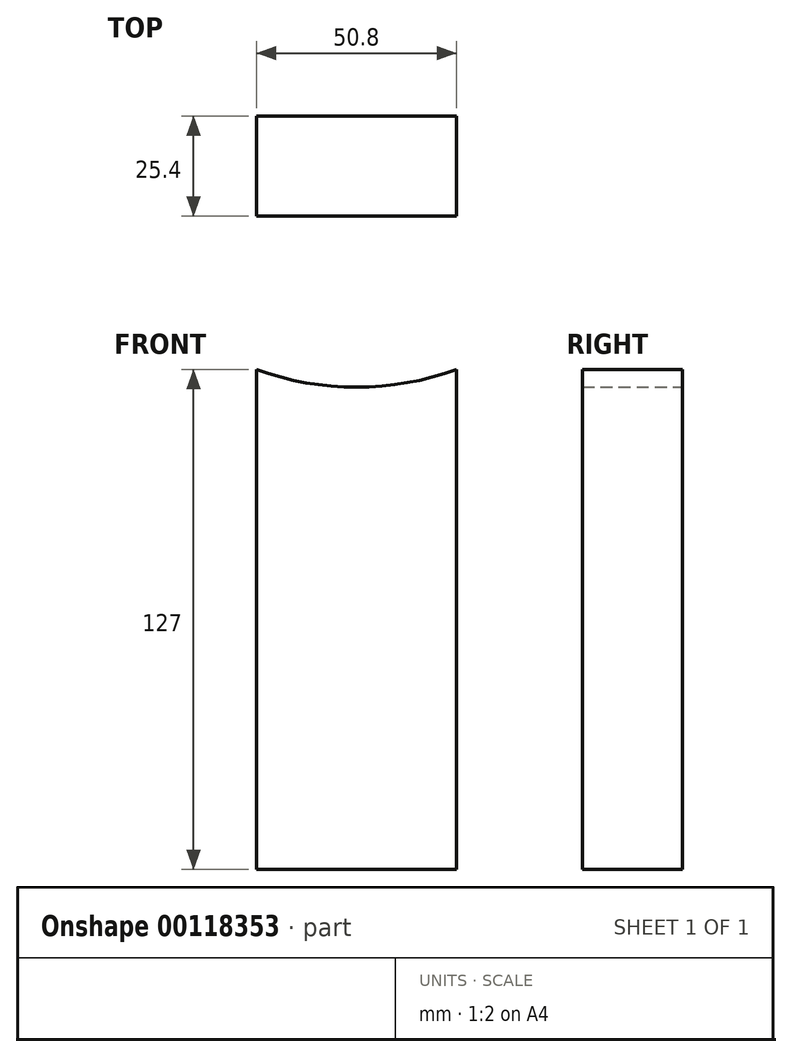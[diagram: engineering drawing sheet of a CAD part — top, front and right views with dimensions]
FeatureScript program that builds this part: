
annotation { "Feature Type Name" : "Feature", "Feature Type Description" : "" }
export const myFeature = defineFeature(function(context is Context, id is Id, definition is map)
    precondition{}
    {
        {
            var Q0;
            Q0=qCreatedBy(makeId("Front.planeOp"),FACE);
            var sketch = newSketch(context, id + "F0", { "sketchPlane" : qUnion([Q0])});
            skLineSegment(sketch, "E0.top", {"start": v(-41.57, -90.75) * mm, "end": v(9.23, -90.75) * mm});
            skLineSegment(sketch, "E0.left", {"start": v(-41.57, 36.25) * mm, "end": v(-41.57, -90.75) * mm});
            skLineSegment(sketch, "E0.right", {"start": v(9.23, 36.25) * mm, "end": v(9.23, -90.75) * mm});
            skArc(sketch, "E1", {"start": v(-41.57, 36.25) * mm, "mid": v(-16.17, 31.77) * mm, "end": v(9.23, 36.25) * mm});
            skSolve(sketch);
        }
        {
            var Q0;
            Q0 = qSketchRegion(id + "F0", true);
            extrude(context, id + "F1", {"entities" : qUnion([Q0]), "depth" : 25.4 * mm});
        }
    });
